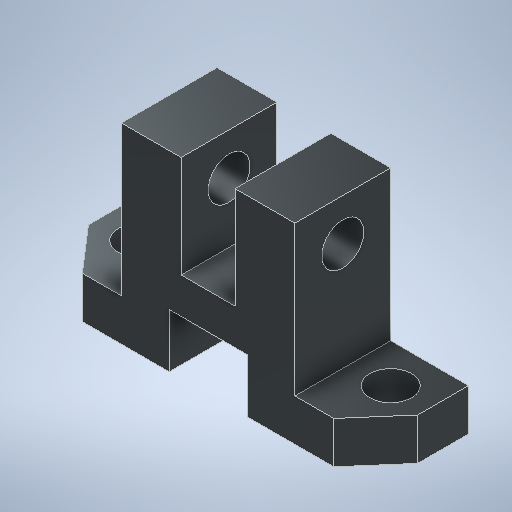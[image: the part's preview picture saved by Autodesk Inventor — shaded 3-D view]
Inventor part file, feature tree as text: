
AUTODESK INVENTOR PART (.ipt)
format: ipt  version: 2025.2 (Build 292293000, 293)  size: 412,672 bytes
history: native  units: in
note: dims shown in document units (in); Inventor stores cm internally (conversion verified against a paired STEP export)
features: extrude x8, sketch x8, projected_geometry x1
ambient origin geometry x8: Origin, YZ Plane, XZ Plane, XY Plane, X Axis, Y Axis, Z Axis, Center Point
bodies: Solid1 (feature_tree)
feature tree (17):
  extrude  "Extrusion1"  Depth=1.2598in
  extrude  "Extrusion2"  Depth=0.3543in
  extrude  "Extrusion3"  Depth=0.315in
  extrude  "Extrusion4"  Depth=0.6693in
  extrude  "Extrusion5"  Depth=0.2756in
  extrude  "Extrusion6"  Depth=0.2756in
  extrude  "Extrusion7"  Depth=0.2756in
  extrude  "Extrusion8"  Depth=0.6299in
  sketch  "Sketch1"  dims[d0=1.1417in d1=1.2598in]
  sketch  "Sketch2"  dims[d2=0.3937in d3=0.3543in d4=0.3937in d8=0.3543in]
  sketch  "Sketch3"  dims[d9=0.315in d10=0.315in]
  sketch  "Sketch4"  dims[d11=0.3543in d12=0.6693in]
  sketch  "Sketch5"  dims[d13=0.6299in d14=0.0in d15=0.2756in]
  projected_geometry  "Projected Loop1"
  sketch  "Sketch6"  dims[d16=0.5118in d17=0.0in d18=0.2756in]
  sketch  "Sketch7"  dims[d19=0.5118in d20=0.0in d21=0.2756in]
  sketch  "Sketch8"  dims[d22=0.2756in d23=0.6299in d24=0.315in d25=0.0in d26=0.0in d28=0.3937in d29=0.2953in d36=0.2756in d37=0.0in d38=0.0in d39=0.2559in d40=0.2953in d41=0.0in d42=0.0in d44=0.2756in d46=0.2953in d47=0.2559in d48=0.0in d49=0.0in d50=0.2559in d51=0.2953in d52=0.0in d53=0.0in]
